# Revit family: TrashBox-WasteBin-3Lt-5Lt-12Lt-Vitra-ArkitektaSeries-A44054+A44055+A44056
name_source: partatom
category: Plumbing Fixtures
revit_build: Autodesk Revit 2017 (Build: 20160225_1515(x64)
units: mm (PartAtom-declared; Revit-internal decimal feet)

## family parameters
Cut with Voids When Loaded = No
Host = Face
OmniClass Number = 23.45.55.17
OmniClass Title = Mixing Faucets
Part Type = Normal
Room Calculation Point = No
Round Connector Dimension = Use Diameter
Shared = Yes

## types (20) — shared parameters
BIMobject category = Sanitary - Accessories
CW Connection = No
Coating Material = Chrome
Color = Chrome
Date of publishing = 2003
Depth(mm) = 180 mm  [stored 0.590551 ft]
Design country = Turkey
HW Connection = No
IFC Classification = Furnishing Element
Manufacturer = Vitra
Manufacturer name = Vitra
Masterformat 2014 Code = 11 82 13
Masterformat 2014 Description = Solid Waste Bins
MountingType = Floor-Standing
NBS Referans Code = 35-10-97
NBS Referans Description = Waste Bins
Nominal height = 0.000
Nominal width = 0.000
OmniClass Code = 23-21 17 11
OmniClass Description = Interior Waste Bins
Product Type = Waste Bins
Product certification = https://vitraglobal.com
Product family = ArkitektaSeries
Product group = Trash Box
UNSPSC Code = 56
UNSPSC Description = Furniture and Furnishings
URL = https://vitraglobal.com
Uniclass 1.4 Code = L7235
Uniclass 1.4 Description = Waste disposal units
Uniclass 2.0 Code = PR-35-10-97
Uniclass 2.0 Description = Waste Bins
Uniclass 2015 Code = Pr_40_50_07_96
Uniclass 2015 Name = Waste bins
Uniformat II Description = EQUIPMENT & FURNISHINGS
Warranty Period (Year) = 5
Weight Net (kg) = 0,820
Width(mm) = 180 mm  [stored 0.590551 ft]
Youtube = https://www.youtube.com
zero-valued in all types: CWFU, Cost, Default Elevation, HWFU, WFU

## per-type parameters (varying)
| type | Article No. (default) | Description | Diameter (mm) | Height(mm) | Hinge High (mm) | HingeDiameter | Model | PedalDiameter | Product SKU | Product data url | Technical description |
| TrashBox-WasteBin-3Lt-Vitra-ArkitektaSeries-A44054 | A44054 | Arkitekta Trash Box 3Lt | 90 mm | 262 mm  [stored 0.85958 ft] | 178 mm  [stored 0.58399 ft] | 75 mm  [stored 0.246063 ft] | A44054 | 75 mm  [stored 0.246063 ft] | A44054 | https://www.vitra.com.tr | https://www.vitra.com.tr |
| TrashBox-WasteBin-5Lt-Vitra-ArkitektaSeries-A44055 | A44055 | Arkitekta Trash Box 5Lt | 90 mm | 295 mm  [stored 0.967848 ft] | 211 mm  [stored 0.692257 ft] | 75 mm  [stored 0.246063 ft] | A44055 | 75 mm  [stored 0.246063 ft] | A44055 | https://www.vitra.com.tr | https://www.vitra.com.tr |
| TrashBox-WasteBin-12Lt-Vitra-ArkitektaSeries-A44056 | A44056 | Arkitekta Trash Box 12Lt | 130 mm  [stored 0.426509 ft] | 365 mm  [stored 1.19751 ft] | 281 mm  [stored 0.921916 ft] | 115 mm  [stored 0.377297 ft] | A44056 | 115 mm  [stored 0.377297 ft] | A44056 | https://www.vitra.com.tr | https://www.vitra.com.tr |
| TrashBox-WasteBin-3Lt-Vitra-ArkitektaSeries-A44054EXP | A44054EXP | Arkitekta Trash Box 3Lt | 90 mm | 262 mm  [stored 0.85958 ft] | 178 mm  [stored 0.58399 ft] | 75 mm  [stored 0.246063 ft] | A44054EXP | 75 mm  [stored 0.246063 ft] | A44054EXP | https://www.vitraglobal.com | https://www.vitraglobal.com |
| TrashBox-WasteBin-5Lt-Vitra-ArkitektaSeries-A44055EXP | A44055EXP | Arkitekta Trash Box 5Lt | 90 mm | 295 mm  [stored 0.967848 ft] | 211 mm  [stored 0.692257 ft] | 75 mm  [stored 0.246063 ft] | A44055EXP | 75 mm  [stored 0.246063 ft] | A44055EXP | https://www.vitraglobal.com | https://www.vitraglobal.com |
| TrashBox-WasteBin-12Lt-Vitra-ArkitektaSeries-A44056EXP | A44056EXP | Arkitekta Trash Box 12Lt | 130 mm  [stored 0.426509 ft] | 365 mm  [stored 1.19751 ft] | 281 mm  [stored 0.921916 ft] | 115 mm  [stored 0.377297 ft] | A44056EXP | 115 mm  [stored 0.377297 ft] | A44056EXP | https://www.vitraglobal.com | https://www.vitraglobal.com |
| TrashBox-WasteBin-3Lt-Vitra-ArkitektaSeries-A44054VUK | A44054VUK | Arkitekta Trash Box 3Lt | 90 mm | 262 mm  [stored 0.85958 ft] | 178 mm  [stored 0.58399 ft] | 75 mm  [stored 0.246063 ft] | A44054VUK | 75 mm  [stored 0.246063 ft] | A44054VUK | https://www.vitra.co.uk | https://www.vitra.co.uk |
| TrashBox-WasteBin-5Lt-Vitra-ArkitektaSeries-A44055VUK | A44055VUK | Arkitekta Trash Box 5Lt | 90 mm | 295 mm  [stored 0.967848 ft] | 211 mm  [stored 0.692257 ft] | 75 mm  [stored 0.246063 ft] | A44055VUK | 75 mm  [stored 0.246063 ft] | A44055VUK | https://www.vitraglobal.com | https://www.vitraglobal.com |
| TrashBox-WasteBin-12Lt-Vitra-ArkitektaSeries-A44056VUK | A44056VUK | Arkitekta Trash Box 12Lt | 130 mm  [stored 0.426509 ft] | 365 mm  [stored 1.19751 ft] | 281 mm  [stored 0.921916 ft] | 115 mm  [stored 0.377297 ft] | A44056VUK | 115 mm  [stored 0.377297 ft] | A44056VUK | https://www.vitraglobal.com | https://www.vitraglobal.com |
| TrashBox-WasteBin-3Lt-Vitra-ArkitektaSeries-A44054EKM | A44054EKM | Arkitekta Trash Box 3Lt | 90 mm | 262 mm  [stored 0.85958 ft] | 178 mm  [stored 0.58399 ft] | 75 mm  [stored 0.246063 ft] | A44054EKM | 75 mm  [stored 0.246063 ft] | A44054EKM | https://www.vitra.co.uk | https://www.vitra.co.uk |
| TrashBox-WasteBin-3Lt-Vitra-ArkitektaSeries-A4405401 | A4405401 | Arkitekta Trash Box 3Lt | 90 mm | 262 mm  [stored 0.85958 ft] | 178 mm  [stored 0.58399 ft] | 75 mm  [stored 0.246063 ft] | A4405401 | 75 mm  [stored 0.246063 ft] | A4405401 | https://www.vitra.co.uk | https://www.vitra.co.uk |
| TrashBox-WasteBin-3Lt-Vitra-ArkitektaSeries-A4405499 | A4405499 | Arkitekta Trash Box 3Lt | 90 mm | 262 mm  [stored 0.85958 ft] | 178 mm  [stored 0.58399 ft] | 75 mm  [stored 0.246063 ft] | A4405499 | 75 mm  [stored 0.246063 ft] | A4405499 | https://www.vitra.co.uk | https://www.vitra.co.uk |
| TrashBox-WasteBin-3Lt-Vitra-ArkitektaSeries-A44054CER | A44054CER | Arkitekta Trash Box 3Lt | 90 mm | 262 mm  [stored 0.85958 ft] | 178 mm  [stored 0.58399 ft] | 75 mm  [stored 0.246063 ft] | A44054CER | 75 mm  [stored 0.246063 ft] | A44054CER | https://www.vitra.co.uk | https://www.vitra.co.uk |
| TrashBox-WasteBin-5Lt-Vitra-ArkitektaSeries-A4405501 | A4405501 | Arkitekta Trash Box 5Lt | 90 mm | 295 mm  [stored 0.967848 ft] | 211 mm  [stored 0.692257 ft] | 75 mm  [stored 0.246063 ft] | A4405501 | 75 mm  [stored 0.246063 ft] | A4405501 | https://www.vitraglobal.com | https://www.vitraglobal.com |
| TrashBox-WasteBin-5Lt-Vitra-ArkitektaSeries-A4405599 | A4405599 | Arkitekta Trash Box 5Lt | 90 mm | 295 mm  [stored 0.967848 ft] | 211 mm  [stored 0.692257 ft] | 75 mm  [stored 0.246063 ft] | A4405599 | 75 mm  [stored 0.246063 ft] | A4405599 | https://www.vitraglobal.com | https://www.vitraglobal.com |
| TrashBox-WasteBin-5Lt-Vitra-ArkitektaSeries-A44055CER | A44055CER | Arkitekta Trash Box 5Lt | 90 mm | 295 mm  [stored 0.967848 ft] | 211 mm  [stored 0.692257 ft] | 75 mm  [stored 0.246063 ft] | A44055CER | 75 mm  [stored 0.246063 ft] | A44055CER | https://www.vitraglobal.com | https://www.vitraglobal.com |
| TrashBox-WasteBin-5Lt-Vitra-ArkitektaSeries-A44055EKM | A44055EKM | Arkitekta Trash Box 5Lt | 90 mm | 295 mm  [stored 0.967848 ft] | 211 mm  [stored 0.692257 ft] | 75 mm  [stored 0.246063 ft] | A44055EKM | 75 mm  [stored 0.246063 ft] | A44055EKM | https://www.vitraglobal.com | https://www.vitraglobal.com |
| TrashBox-WasteBin-5Lt-Vitra-ArkitektaSeries-A44055TPL | A44055TPL | Arkitekta Trash Box 5Lt | 90 mm | 295 mm  [stored 0.967848 ft] | 211 mm  [stored 0.692257 ft] | 75 mm  [stored 0.246063 ft] | A44055TPL | 75 mm  [stored 0.246063 ft] | A44055TPL | https://www.vitraglobal.com | https://www.vitraglobal.com |
| TrashBox-WasteBin-12Lt-Vitra-ArkitektaSeries-A44056CER | A44056CER | Arkitekta Trash Box 12Lt | 130 mm  [stored 0.426509 ft] | 365 mm  [stored 1.19751 ft] | 281 mm  [stored 0.921916 ft] | 115 mm  [stored 0.377297 ft] | A44056CER | 115 mm  [stored 0.377297 ft] | A44056CER | https://www.vitraglobal.com | https://www.vitraglobal.com |
| TrashBox-WasteBin-12Lt-Vitra-ArkitektaSeries-A44056EKM | A44056EKM | Arkitekta Trash Box 12Lt | 130 mm  [stored 0.426509 ft] | 365 mm  [stored 1.19751 ft] | 281 mm  [stored 0.921916 ft] | 115 mm  [stored 0.377297 ft] | A44056EKM | 115 mm  [stored 0.377297 ft] | A44056EKM | https://www.vitraglobal.com | https://www.vitraglobal.com |

note: [stored X ft] marks values corroborated as IEEE doubles in the binary element streams (Revit-internal decimal feet)

## geometry (parser evidence)
native form markers: Sweep x3
no freeform markers — native parametric forms only
